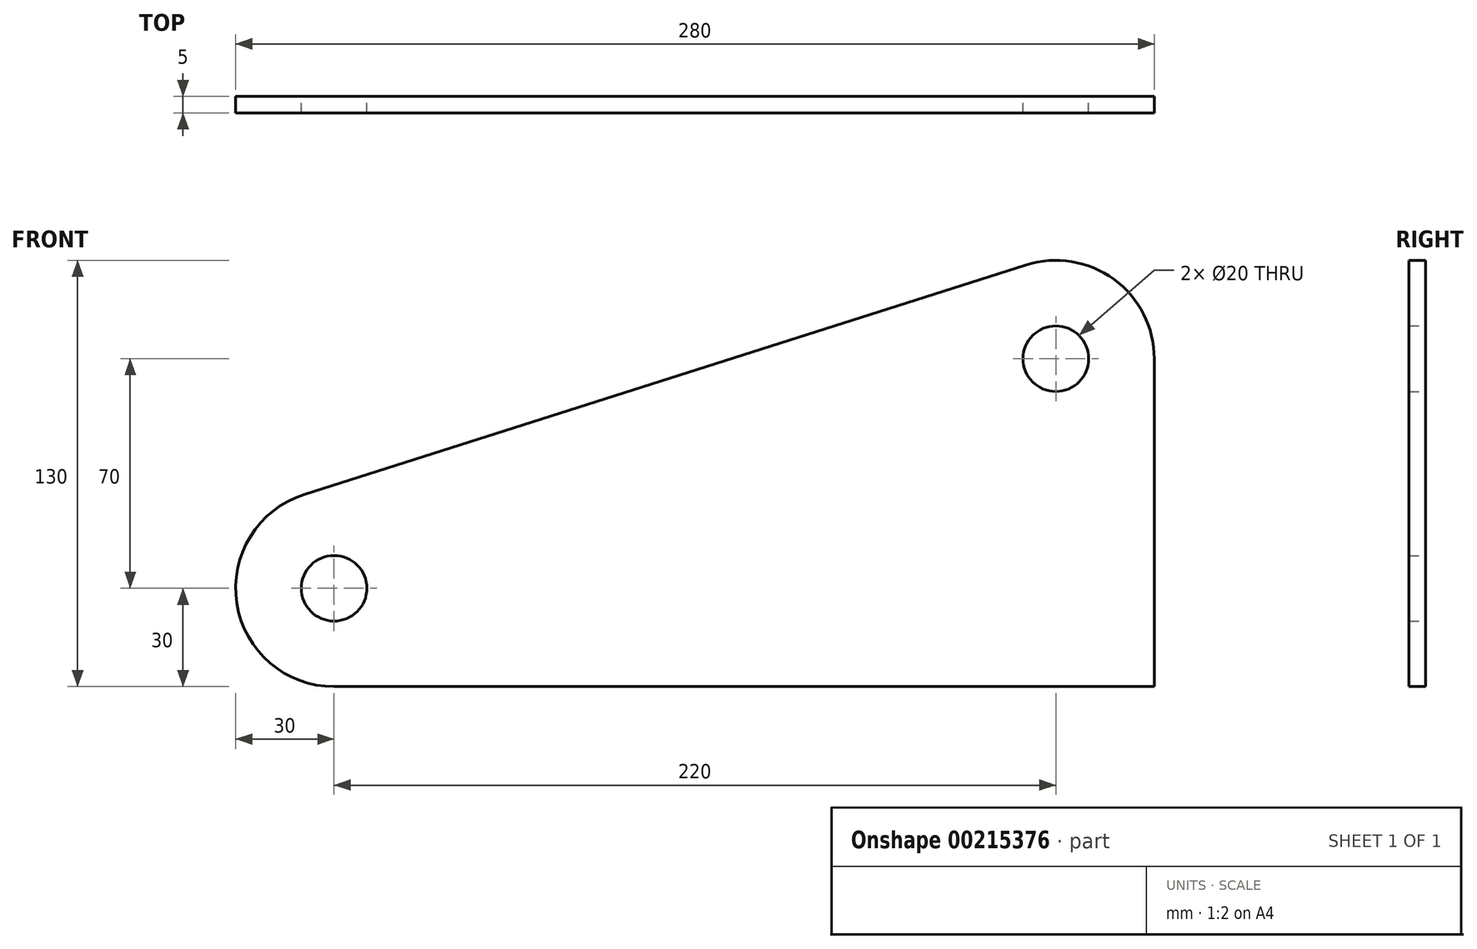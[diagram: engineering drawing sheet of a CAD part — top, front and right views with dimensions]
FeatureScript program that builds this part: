
annotation { "Feature Type Name" : "Feature", "Feature Type Description" : "" }
export const myFeature = defineFeature(function(context is Context, id is Id, definition is map)
    precondition{}
    {
        {
            var Q0;
            Q0=qCreatedBy(makeId("Front.planeOp"),FACE);
            cPlane(context, id + "F0", {"entities" : qUnion([Q0]), "cplaneType" : CPlaneType.OFFSET, "offset" : 25 * mm, "width" : 150 * mm, "height" : 150 * mm});
        }
        {
            var Q0;
            Q0=qCreatedBy(id+"F0.planeOp",FACE);
            var sketch = newSketch(context, id + "F1", { "sketchPlane" : qUnion([Q0])});
            skLineSegment(sketch, "E0", {"start": v(-250, 0) * mm, "end": v(0, 0) * mm});
            skLineSegment(sketch, "E1", {"start": v(0, 0) * mm, "end": v(0, 100) * mm});
            skLineSegment(sketch, "E2", {"start": v(-39.1, 128.59) * mm, "end": v(-259.1, 58.59) * mm});
            skArc(sketch, "E3", {"start": v(-259.1, 58.59) * mm, "mid": v(-279.64, 25.4) * mm, "end": v(-250, 0) * mm});
            skArc(sketch, "E4", {"start": v(-39.1, 128.59) * mm, "mid": v(-12.3, 124.22) * mm, "end": v(0, 100) * mm});
            skCircle(sketch, "E5", {"center": v(-30, 100) * mm, "radius": 10 * mm});
            skCircle(sketch, "E6", {"center": v(-250, 30) * mm, "radius": 10 * mm});
            skSolve(sketch);
        }
        {
            var Q0;
            Q0=makeQuery(id+"F1.imprint","IMPRINT",FACE,{"disambiguationData":[TD([[makeQuery(id+"F1.imprint","IMPRINT",EDGE,{"derivedFrom":sQuery(id+"F1.wireOp",EDGE,"E0")}),1.0]])]});
            extrude(context, id + "F2", {"entities" : qUnion([Q0]), "endBound" : BoundingType.SYMMETRIC, "depth" : 5 * mm});
        }
    });
